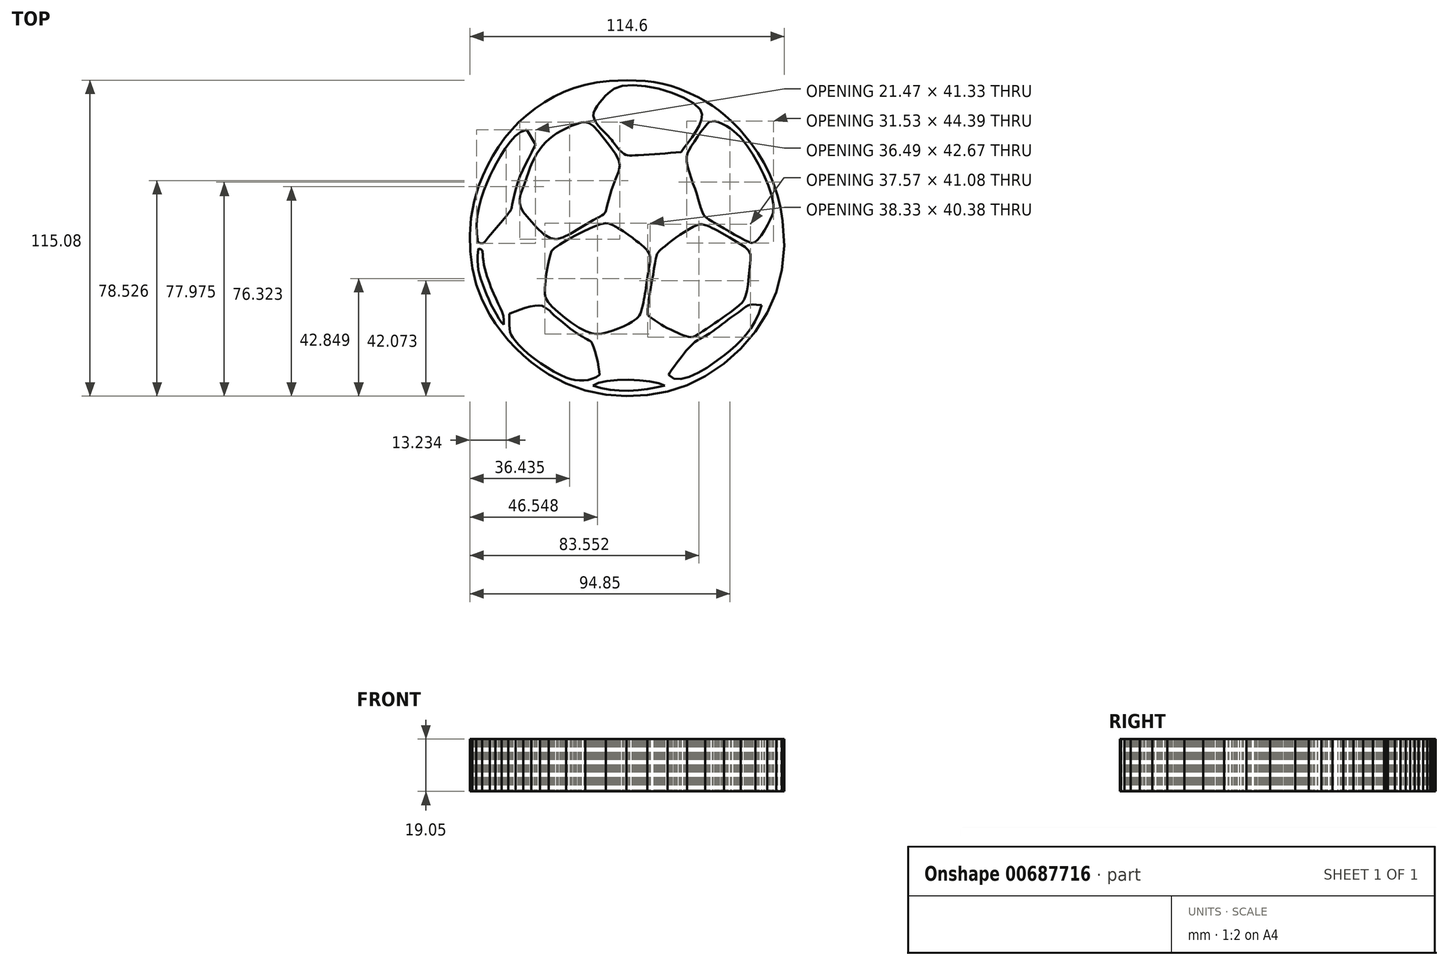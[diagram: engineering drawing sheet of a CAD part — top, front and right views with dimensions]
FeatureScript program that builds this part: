
annotation { "Feature Type Name" : "Feature", "Feature Type Description" : "" }
export const myFeature = defineFeature(function(context is Context, id is Id, definition is map)
    precondition{}
    {
        {
            var Q0;
            Q0=qCreatedBy(makeId("Top.planeOp"),FACE);
            var sketch = newSketch(context, id + "F0", { "sketchPlane" : qUnion([Q0])});
            skLineSegment(sketch, "E0", {"start": v(-6.43, 57.28) * mm, "end": v(-10.96, 56.75) * mm});
            skLineSegment(sketch, "E1", {"start": v(-10.96, 56.75) * mm, "end": v(-15.2, 55.9) * mm});
            skLineSegment(sketch, "E2", {"start": v(-15.2, 55.9) * mm, "end": v(-19.2, 54.74) * mm});
            skLineSegment(sketch, "E3", {"start": v(-19.2, 54.74) * mm, "end": v(-23, 53.29) * mm});
            skLineSegment(sketch, "E4", {"start": v(-23, 53.29) * mm, "end": v(-26.62, 51.54) * mm});
            skLineSegment(sketch, "E5", {"start": v(-26.62, 51.54) * mm, "end": v(-30.1, 49.5) * mm});
            skLineSegment(sketch, "E6", {"start": v(-30.1, 49.5) * mm, "end": v(-33.5, 47.2) * mm});
            skLineSegment(sketch, "E7", {"start": v(-33.5, 47.2) * mm, "end": v(-36.82, 44.64) * mm});
            skLineSegment(sketch, "E8", {"start": v(-36.82, 44.64) * mm, "end": v(-39.47, 42.27) * mm});
            skLineSegment(sketch, "E9", {"start": v(-39.47, 42.27) * mm, "end": v(-42.04, 39.56) * mm});
            skLineSegment(sketch, "E10", {"start": v(-42.04, 39.56) * mm, "end": v(-44.5, 36.54) * mm});
            skLineSegment(sketch, "E11", {"start": v(-44.5, 36.54) * mm, "end": v(-46.81, 33.3) * mm});
            skLineSegment(sketch, "E12", {"start": v(-46.81, 33.3) * mm, "end": v(-48.96, 29.86) * mm});
            skLineSegment(sketch, "E13", {"start": v(-48.96, 29.86) * mm, "end": v(-50.9, 26.3) * mm});
            skLineSegment(sketch, "E14", {"start": v(-50.9, 26.3) * mm, "end": v(-52.6, 22.69) * mm});
            skLineSegment(sketch, "E15", {"start": v(-52.6, 22.69) * mm, "end": v(-54.02, 19.06) * mm});
            skLineSegment(sketch, "E16", {"start": v(-54.02, 19.06) * mm, "end": v(-55.72, 13.29) * mm});
            skLineSegment(sketch, "E17", {"start": v(-55.72, 13.29) * mm, "end": v(-56.82, 7.32) * mm});
            skLineSegment(sketch, "E18", {"start": v(-56.82, 7.32) * mm, "end": v(-57.3, 1.24) * mm});
            skLineSegment(sketch, "E19", {"start": v(-57.3, 1.24) * mm, "end": v(-57.16, -4.87) * mm});
            skLineSegment(sketch, "E20", {"start": v(-57.16, -4.87) * mm, "end": v(-56.37, -10.92) * mm});
            skLineSegment(sketch, "E21", {"start": v(-56.37, -10.92) * mm, "end": v(-54.92, -16.83) * mm});
            skLineSegment(sketch, "E22", {"start": v(-54.92, -16.83) * mm, "end": v(-52.82, -22.52) * mm});
            skLineSegment(sketch, "E23", {"start": v(-52.82, -22.52) * mm, "end": v(-50.03, -27.9) * mm});
            skLineSegment(sketch, "E24", {"start": v(-50.03, -27.9) * mm, "end": v(-47.95, -31.1) * mm});
            skLineSegment(sketch, "E25", {"start": v(-47.95, -31.1) * mm, "end": v(-45.67, -34.2) * mm});
            skLineSegment(sketch, "E26", {"start": v(-45.67, -34.2) * mm, "end": v(-43.2, -37.17) * mm});
            skLineSegment(sketch, "E27", {"start": v(-43.2, -37.17) * mm, "end": v(-40.57, -40) * mm});
            skLineSegment(sketch, "E28", {"start": v(-40.57, -40) * mm, "end": v(-37.77, -42.66) * mm});
            skLineSegment(sketch, "E29", {"start": v(-37.77, -42.66) * mm, "end": v(-34.84, -45.16) * mm});
            skLineSegment(sketch, "E30", {"start": v(-34.84, -45.16) * mm, "end": v(-31.77, -47.49) * mm});
            skLineSegment(sketch, "E31", {"start": v(-31.77, -47.49) * mm, "end": v(-28.58, -49.63) * mm});
            skLineSegment(sketch, "E32", {"start": v(-28.58, -49.63) * mm, "end": v(-22.14, -53.01) * mm});
            skLineSegment(sketch, "E33", {"start": v(-22.14, -53.01) * mm, "end": v(-15.14, -55.46) * mm});
            skLineSegment(sketch, "E34", {"start": v(-15.14, -55.46) * mm, "end": v(-7.77, -56.97) * mm});
            skLineSegment(sketch, "E35", {"start": v(-7.77, -56.97) * mm, "end": v(-0.2, -57.54) * mm});
            skLineSegment(sketch, "E36", {"start": v(-0.2, -57.54) * mm, "end": v(7.4, -57.17) * mm});
            skLineSegment(sketch, "E37", {"start": v(7.4, -57.17) * mm, "end": v(14.82, -55.84) * mm});
            skLineSegment(sketch, "E38", {"start": v(14.82, -55.84) * mm, "end": v(21.9, -53.57) * mm});
            skLineSegment(sketch, "E39", {"start": v(21.9, -53.57) * mm, "end": v(28.46, -50.35) * mm});
            skLineSegment(sketch, "E40", {"start": v(28.46, -50.35) * mm, "end": v(35.3, -45.68) * mm});
            skLineSegment(sketch, "E41", {"start": v(35.3, -45.68) * mm, "end": v(41.42, -40.23) * mm});
            skLineSegment(sketch, "E42", {"start": v(41.42, -40.23) * mm, "end": v(46.71, -34.04) * mm});
            skLineSegment(sketch, "E43", {"start": v(46.71, -34.04) * mm, "end": v(51.06, -27.15) * mm});
            skLineSegment(sketch, "E44", {"start": v(51.06, -27.15) * mm, "end": v(54.35, -19.62) * mm});
            skLineSegment(sketch, "E45", {"start": v(54.35, -19.62) * mm, "end": v(56.47, -11.5) * mm});
            skLineSegment(sketch, "E46", {"start": v(56.47, -11.5) * mm, "end": v(57.3, -2.82) * mm});
            skLineSegment(sketch, "E47", {"start": v(57.3, -2.82) * mm, "end": v(56.73, 6.35) * mm});
            skLineSegment(sketch, "E48", {"start": v(56.73, 6.35) * mm, "end": v(55.88, 11.3) * mm});
            skLineSegment(sketch, "E49", {"start": v(55.88, 11.3) * mm, "end": v(54.78, 15.82) * mm});
            skLineSegment(sketch, "E50", {"start": v(54.78, 15.82) * mm, "end": v(53.41, 19.97) * mm});
            skLineSegment(sketch, "E51", {"start": v(53.41, 19.97) * mm, "end": v(51.77, 23.85) * mm});
            skLineSegment(sketch, "E52", {"start": v(51.77, 23.85) * mm, "end": v(49.84, 27.53) * mm});
            skLineSegment(sketch, "E53", {"start": v(49.84, 27.53) * mm, "end": v(47.6, 31.1) * mm});
            skLineSegment(sketch, "E54", {"start": v(47.6, 31.1) * mm, "end": v(45.06, 34.62) * mm});
            skLineSegment(sketch, "E55", {"start": v(45.06, 34.62) * mm, "end": v(42.2, 38.18) * mm});
            skLineSegment(sketch, "E56", {"start": v(42.2, 38.18) * mm, "end": v(41.76, 38.73) * mm});
            skLineSegment(sketch, "E57", {"start": v(41.76, 38.73) * mm, "end": v(41.43, 39.18) * mm});
            skLineSegment(sketch, "E58", {"start": v(41.43, 39.18) * mm, "end": v(41.26, 39.4) * mm});
            skLineSegment(sketch, "E59", {"start": v(41.26, 39.4) * mm, "end": v(41.07, 39.63) * mm});
            skLineSegment(sketch, "E60", {"start": v(41.07, 39.63) * mm, "end": v(40.85, 39.87) * mm});
            skLineSegment(sketch, "E61", {"start": v(40.85, 39.87) * mm, "end": v(40.58, 40.14) * mm});
            skLineSegment(sketch, "E62", {"start": v(40.58, 40.14) * mm, "end": v(37.99, 42.62) * mm});
            skLineSegment(sketch, "E63", {"start": v(37.99, 42.62) * mm, "end": v(35.66, 44.75) * mm});
            skLineSegment(sketch, "E64", {"start": v(35.66, 44.75) * mm, "end": v(33.45, 46.62) * mm});
            skLineSegment(sketch, "E65", {"start": v(33.45, 46.62) * mm, "end": v(31.21, 48.3) * mm});
            skLineSegment(sketch, "E66", {"start": v(31.21, 48.3) * mm, "end": v(28.79, 49.85) * mm});
            skLineSegment(sketch, "E67", {"start": v(28.79, 49.85) * mm, "end": v(26.03, 51.36) * mm});
            skLineSegment(sketch, "E68", {"start": v(26.03, 51.36) * mm, "end": v(22.78, 52.89) * mm});
            skLineSegment(sketch, "E69", {"start": v(22.78, 52.89) * mm, "end": v(18.9, 54.52) * mm});
            skLineSegment(sketch, "E70", {"start": v(18.9, 54.52) * mm, "end": v(16.04, 55.5) * mm});
            skLineSegment(sketch, "E71", {"start": v(16.04, 55.5) * mm, "end": v(13.02, 56.29) * mm});
            skLineSegment(sketch, "E72", {"start": v(13.02, 56.29) * mm, "end": v(9.86, 56.86) * mm});
            skLineSegment(sketch, "E73", {"start": v(9.86, 56.86) * mm, "end": v(6.63, 57.25) * mm});
            skLineSegment(sketch, "E74", {"start": v(6.63, 57.25) * mm, "end": v(3.34, 57.47) * mm});
            skLineSegment(sketch, "E75", {"start": v(3.34, 57.47) * mm, "end": v(0.04, 57.54) * mm});
            skLineSegment(sketch, "E76", {"start": v(0.04, 57.54) * mm, "end": v(-3.23, 57.47) * mm});
            skLineSegment(sketch, "E77", {"start": v(-3.23, 57.47) * mm, "end": v(-6.43, 57.28) * mm});
            skLineSegment(sketch, "E78", {"start": v(-7.9, 5.5) * mm, "end": v(-9.76, 5.04) * mm});
            skLineSegment(sketch, "E79", {"start": v(-9.76, 5.04) * mm, "end": v(-12.38, 4.05) * mm});
            skLineSegment(sketch, "E80", {"start": v(-12.38, 4.05) * mm, "end": v(-15.46, 2.67) * mm});
            skLineSegment(sketch, "E81", {"start": v(-15.46, 2.67) * mm, "end": v(-18.7, 1.06) * mm});
            skLineSegment(sketch, "E82", {"start": v(-18.7, 1.06) * mm, "end": v(-21.82, -0.64) * mm});
            skLineSegment(sketch, "E83", {"start": v(-21.82, -0.64) * mm, "end": v(-24.53, -2.26) * mm});
            skLineSegment(sketch, "E84", {"start": v(-24.53, -2.26) * mm, "end": v(-26.52, -3.67) * mm});
            skLineSegment(sketch, "E85", {"start": v(-26.52, -3.67) * mm, "end": v(-27.5, -4.7) * mm});
            skLineSegment(sketch, "E86", {"start": v(-27.5, -4.7) * mm, "end": v(-27.94, -5.93) * mm});
            skLineSegment(sketch, "E87", {"start": v(-27.94, -5.93) * mm, "end": v(-28.43, -7.85) * mm});
            skLineSegment(sketch, "E88", {"start": v(-28.43, -7.85) * mm, "end": v(-28.93, -10.24) * mm});
            skLineSegment(sketch, "E89", {"start": v(-28.93, -10.24) * mm, "end": v(-29.37, -12.9) * mm});
            skLineSegment(sketch, "E90", {"start": v(-29.37, -12.9) * mm, "end": v(-29.72, -15.6) * mm});
            skLineSegment(sketch, "E91", {"start": v(-29.72, -15.6) * mm, "end": v(-29.92, -18.13) * mm});
            skLineSegment(sketch, "E92", {"start": v(-29.92, -18.13) * mm, "end": v(-29.9, -20.26) * mm});
            skLineSegment(sketch, "E93", {"start": v(-29.9, -20.26) * mm, "end": v(-29.64, -21.77) * mm});
            skLineSegment(sketch, "E94", {"start": v(-29.64, -21.77) * mm, "end": v(-28.79, -23.23) * mm});
            skLineSegment(sketch, "E95", {"start": v(-28.79, -23.23) * mm, "end": v(-27.24, -25.01) * mm});
            skLineSegment(sketch, "E96", {"start": v(-27.24, -25.01) * mm, "end": v(-25.16, -26.98) * mm});
            skLineSegment(sketch, "E97", {"start": v(-25.16, -26.98) * mm, "end": v(-22.73, -28.98) * mm});
            skLineSegment(sketch, "E98", {"start": v(-22.73, -28.98) * mm, "end": v(-20.12, -30.9) * mm});
            skLineSegment(sketch, "E99", {"start": v(-20.12, -30.9) * mm, "end": v(-17.48, -32.57) * mm});
            skLineSegment(sketch, "E100", {"start": v(-17.48, -32.57) * mm, "end": v(-15, -33.88) * mm});
            skLineSegment(sketch, "E101", {"start": v(-15, -33.88) * mm, "end": v(-12.84, -34.68) * mm});
            skLineSegment(sketch, "E102", {"start": v(-12.84, -34.68) * mm, "end": v(-11.16, -34.88) * mm});
            skLineSegment(sketch, "E103", {"start": v(-11.16, -34.88) * mm, "end": v(-9.25, -34.74) * mm});
            skLineSegment(sketch, "E104", {"start": v(-9.25, -34.74) * mm, "end": v(-7.2, -34.32) * mm});
            skLineSegment(sketch, "E105", {"start": v(-7.2, -34.32) * mm, "end": v(-5.11, -33.7) * mm});
            skLineSegment(sketch, "E106", {"start": v(-5.11, -33.7) * mm, "end": v(-3.08, -32.92) * mm});
            skLineSegment(sketch, "E107", {"start": v(-3.08, -32.92) * mm, "end": v(-1.18, -32.08) * mm});
            skLineSegment(sketch, "E108", {"start": v(-1.18, -32.08) * mm, "end": v(0.48, -31.23) * mm});
            skLineSegment(sketch, "E109", {"start": v(0.48, -31.23) * mm, "end": v(1.82, -30.44) * mm});
            skLineSegment(sketch, "E110", {"start": v(1.82, -30.44) * mm, "end": v(2.73, -29.84) * mm});
            skLineSegment(sketch, "E111", {"start": v(2.73, -29.84) * mm, "end": v(3.45, -29.3) * mm});
            skLineSegment(sketch, "E112", {"start": v(3.45, -29.3) * mm, "end": v(4.02, -28.78) * mm});
            skLineSegment(sketch, "E113", {"start": v(4.02, -28.78) * mm, "end": v(4.46, -28.22) * mm});
            skLineSegment(sketch, "E114", {"start": v(4.46, -28.22) * mm, "end": v(4.82, -27.56) * mm});
            skLineSegment(sketch, "E115", {"start": v(4.82, -27.56) * mm, "end": v(5.13, -26.74) * mm});
            skLineSegment(sketch, "E116", {"start": v(5.13, -26.74) * mm, "end": v(5.42, -25.73) * mm});
            skLineSegment(sketch, "E117", {"start": v(5.42, -25.73) * mm, "end": v(5.73, -24.45) * mm});
            skLineSegment(sketch, "E118", {"start": v(5.73, -24.45) * mm, "end": v(5.96, -23.4) * mm});
            skLineSegment(sketch, "E119", {"start": v(5.96, -23.4) * mm, "end": v(6.17, -22.34) * mm});
            skLineSegment(sketch, "E120", {"start": v(6.17, -22.34) * mm, "end": v(6.36, -21.29) * mm});
            skLineSegment(sketch, "E121", {"start": v(6.36, -21.29) * mm, "end": v(6.54, -20.23) * mm});
            skLineSegment(sketch, "E122", {"start": v(6.54, -20.23) * mm, "end": v(6.7, -19.17) * mm});
            skLineSegment(sketch, "E123", {"start": v(6.7, -19.17) * mm, "end": v(6.87, -18.11) * mm});
            skLineSegment(sketch, "E124", {"start": v(6.87, -18.11) * mm, "end": v(7.02, -17.05) * mm});
            skLineSegment(sketch, "E125", {"start": v(7.02, -17.05) * mm, "end": v(7.16, -16) * mm});
            skLineSegment(sketch, "E126", {"start": v(7.16, -16) * mm, "end": v(7.65, -12.86) * mm});
            skLineSegment(sketch, "E127", {"start": v(7.65, -12.86) * mm, "end": v(8.09, -10.41) * mm});
            skLineSegment(sketch, "E128", {"start": v(8.09, -10.41) * mm, "end": v(8.37, -8.5) * mm});
            skLineSegment(sketch, "E129", {"start": v(8.37, -8.5) * mm, "end": v(8.41, -6.98) * mm});
            skLineSegment(sketch, "E130", {"start": v(8.41, -6.98) * mm, "end": v(8.12, -5.7) * mm});
            skLineSegment(sketch, "E131", {"start": v(8.12, -5.7) * mm, "end": v(7.4, -4.48) * mm});
            skLineSegment(sketch, "E132", {"start": v(7.4, -4.48) * mm, "end": v(6.16, -3.2) * mm});
            skLineSegment(sketch, "E133", {"start": v(6.16, -3.2) * mm, "end": v(4.31, -1.68) * mm});
            skLineSegment(sketch, "E134", {"start": v(4.31, -1.68) * mm, "end": v(3.38, -0.95) * mm});
            skLineSegment(sketch, "E135", {"start": v(3.38, -0.95) * mm, "end": v(2.04, 0.08) * mm});
            skLineSegment(sketch, "E136", {"start": v(2.04, 0.08) * mm, "end": v(0.42, 1.3) * mm});
            skLineSegment(sketch, "E137", {"start": v(0.42, 1.3) * mm, "end": v(-1.38, 2.56) * mm});
            skLineSegment(sketch, "E138", {"start": v(-1.38, 2.56) * mm, "end": v(-3.23, 3.74) * mm});
            skLineSegment(sketch, "E139", {"start": v(-3.23, 3.74) * mm, "end": v(-5, 4.7) * mm});
            skLineSegment(sketch, "E140", {"start": v(-5, 4.7) * mm, "end": v(-6.6, 5.34) * mm});
            skLineSegment(sketch, "E141", {"start": v(-6.6, 5.34) * mm, "end": v(-7.9, 5.5) * mm});
            skLineSegment(sketch, "E142", {"start": v(25.64, 4.87) * mm, "end": v(24.21, 4.2) * mm});
            skLineSegment(sketch, "E143", {"start": v(24.21, 4.2) * mm, "end": v(22.63, 3.34) * mm});
            skLineSegment(sketch, "E144", {"start": v(22.63, 3.34) * mm, "end": v(20.97, 2.33) * mm});
            skLineSegment(sketch, "E145", {"start": v(20.97, 2.33) * mm, "end": v(19.3, 1.24) * mm});
            skLineSegment(sketch, "E146", {"start": v(19.3, 1.24) * mm, "end": v(17.67, 0.13) * mm});
            skLineSegment(sketch, "E147", {"start": v(17.67, 0.13) * mm, "end": v(16.18, -0.96) * mm});
            skLineSegment(sketch, "E148", {"start": v(16.18, -0.96) * mm, "end": v(14.88, -1.98) * mm});
            skLineSegment(sketch, "E149", {"start": v(14.88, -1.98) * mm, "end": v(13.84, -2.85) * mm});
            skLineSegment(sketch, "E150", {"start": v(13.84, -2.85) * mm, "end": v(12.97, -3.6) * mm});
            skLineSegment(sketch, "E151", {"start": v(12.97, -3.6) * mm, "end": v(12.28, -4.17) * mm});
            skLineSegment(sketch, "E152", {"start": v(12.28, -4.17) * mm, "end": v(11.74, -4.65) * mm});
            skLineSegment(sketch, "E153", {"start": v(11.74, -4.65) * mm, "end": v(11.32, -5.15) * mm});
            skLineSegment(sketch, "E154", {"start": v(11.32, -5.15) * mm, "end": v(10.98, -5.75) * mm});
            skLineSegment(sketch, "E155", {"start": v(10.98, -5.75) * mm, "end": v(10.7, -6.55) * mm});
            skLineSegment(sketch, "E156", {"start": v(10.7, -6.55) * mm, "end": v(10.45, -7.64) * mm});
            skLineSegment(sketch, "E157", {"start": v(10.45, -7.64) * mm, "end": v(10.19, -9.12) * mm});
            skLineSegment(sketch, "E158", {"start": v(10.19, -9.12) * mm, "end": v(9.87, -11) * mm});
            skLineSegment(sketch, "E159", {"start": v(9.87, -11) * mm, "end": v(9.5, -13.15) * mm});
            skLineSegment(sketch, "E160", {"start": v(9.5, -13.15) * mm, "end": v(9.1, -15.47) * mm});
            skLineSegment(sketch, "E161", {"start": v(9.1, -15.47) * mm, "end": v(8.69, -17.88) * mm});
            skLineSegment(sketch, "E162", {"start": v(8.69, -17.88) * mm, "end": v(8.3, -20.26) * mm});
            skLineSegment(sketch, "E163", {"start": v(8.3, -20.26) * mm, "end": v(7.95, -22.52) * mm});
            skLineSegment(sketch, "E164", {"start": v(7.95, -22.52) * mm, "end": v(7.67, -24.56) * mm});
            skLineSegment(sketch, "E165", {"start": v(7.67, -24.56) * mm, "end": v(7.5, -26.3) * mm});
            skLineSegment(sketch, "E166", {"start": v(7.5, -26.3) * mm, "end": v(7.47, -26.91) * mm});
            skLineSegment(sketch, "E167", {"start": v(7.47, -26.91) * mm, "end": v(7.48, -27.38) * mm});
            skLineSegment(sketch, "E168", {"start": v(7.48, -27.38) * mm, "end": v(7.55, -27.74) * mm});
            skLineSegment(sketch, "E169", {"start": v(7.55, -27.74) * mm, "end": v(7.69, -28.03) * mm});
            skLineSegment(sketch, "E170", {"start": v(7.69, -28.03) * mm, "end": v(7.89, -28.27) * mm});
            skLineSegment(sketch, "E171", {"start": v(7.89, -28.27) * mm, "end": v(8.16, -28.51) * mm});
            skLineSegment(sketch, "E172", {"start": v(8.16, -28.51) * mm, "end": v(8.52, -28.78) * mm});
            skLineSegment(sketch, "E173", {"start": v(8.52, -28.78) * mm, "end": v(8.97, -29.1) * mm});
            skLineSegment(sketch, "E174", {"start": v(8.97, -29.1) * mm, "end": v(10.18, -30) * mm});
            skLineSegment(sketch, "E175", {"start": v(10.18, -30) * mm, "end": v(11.33, -30.78) * mm});
            skLineSegment(sketch, "E176", {"start": v(11.33, -30.78) * mm, "end": v(12.44, -31.47) * mm});
            skLineSegment(sketch, "E177", {"start": v(12.44, -31.47) * mm, "end": v(13.54, -32.1) * mm});
            skLineSegment(sketch, "E178", {"start": v(13.54, -32.1) * mm, "end": v(14.67, -32.7) * mm});
            skLineSegment(sketch, "E179", {"start": v(14.67, -32.7) * mm, "end": v(15.87, -33.29) * mm});
            skLineSegment(sketch, "E180", {"start": v(15.87, -33.29) * mm, "end": v(17.16, -33.89) * mm});
            skLineSegment(sketch, "E181", {"start": v(17.16, -33.89) * mm, "end": v(18.59, -34.53) * mm});
            skLineSegment(sketch, "E182", {"start": v(18.59, -34.53) * mm, "end": v(19.6, -34.98) * mm});
            skLineSegment(sketch, "E183", {"start": v(19.6, -34.98) * mm, "end": v(20.55, -35.4) * mm});
            skLineSegment(sketch, "E184", {"start": v(20.55, -35.4) * mm, "end": v(21.46, -35.73) * mm});
            skLineSegment(sketch, "E185", {"start": v(21.46, -35.73) * mm, "end": v(22.35, -35.94) * mm});
            skLineSegment(sketch, "E186", {"start": v(22.35, -35.94) * mm, "end": v(23.24, -36) * mm});
            skLineSegment(sketch, "E187", {"start": v(23.24, -36) * mm, "end": v(24.15, -35.89) * mm});
            skLineSegment(sketch, "E188", {"start": v(24.15, -35.89) * mm, "end": v(25.1, -35.55) * mm});
            skLineSegment(sketch, "E189", {"start": v(25.1, -35.55) * mm, "end": v(26.13, -34.95) * mm});
            skLineSegment(sketch, "E190", {"start": v(26.13, -34.95) * mm, "end": v(27.59, -33.95) * mm});
            skLineSegment(sketch, "E191", {"start": v(27.59, -33.95) * mm, "end": v(29.03, -32.96) * mm});
            skLineSegment(sketch, "E192", {"start": v(29.03, -32.96) * mm, "end": v(30.46, -32) * mm});
            skLineSegment(sketch, "E193", {"start": v(30.46, -32) * mm, "end": v(31.88, -31.02) * mm});
            skLineSegment(sketch, "E194", {"start": v(31.88, -31.02) * mm, "end": v(33.3, -30.05) * mm});
            skLineSegment(sketch, "E195", {"start": v(33.3, -30.05) * mm, "end": v(34.72, -29.06) * mm});
            skLineSegment(sketch, "E196", {"start": v(34.72, -29.06) * mm, "end": v(36.14, -28.04) * mm});
            skLineSegment(sketch, "E197", {"start": v(36.14, -28.04) * mm, "end": v(37.57, -26.99) * mm});
            skLineSegment(sketch, "E198", {"start": v(37.57, -26.99) * mm, "end": v(39.4, -25.62) * mm});
            skLineSegment(sketch, "E199", {"start": v(39.4, -25.62) * mm, "end": v(40.82, -24.5) * mm});
            skLineSegment(sketch, "E200", {"start": v(40.82, -24.5) * mm, "end": v(41.9, -23.45) * mm});
            skLineSegment(sketch, "E201", {"start": v(41.9, -23.45) * mm, "end": v(42.69, -22.33) * mm});
            skLineSegment(sketch, "E202", {"start": v(42.69, -22.33) * mm, "end": v(43.27, -20.97) * mm});
            skLineSegment(sketch, "E203", {"start": v(43.27, -20.97) * mm, "end": v(43.7, -19.22) * mm});
            skLineSegment(sketch, "E204", {"start": v(43.7, -19.22) * mm, "end": v(44.05, -16.92) * mm});
            skLineSegment(sketch, "E205", {"start": v(44.05, -16.92) * mm, "end": v(44.38, -13.9) * mm});
            skLineSegment(sketch, "E206", {"start": v(44.38, -13.9) * mm, "end": v(44.78, -10.4) * mm});
            skLineSegment(sketch, "E207", {"start": v(44.78, -10.4) * mm, "end": v(45.04, -7.86) * mm});
            skLineSegment(sketch, "E208", {"start": v(45.04, -7.86) * mm, "end": v(44.95, -6) * mm});
            skLineSegment(sketch, "E209", {"start": v(44.95, -6) * mm, "end": v(44.34, -4.56) * mm});
            skLineSegment(sketch, "E210", {"start": v(44.34, -4.56) * mm, "end": v(43, -3.23) * mm});
            skLineSegment(sketch, "E211", {"start": v(43, -3.23) * mm, "end": v(40.72, -1.73) * mm});
            skLineSegment(sketch, "E212", {"start": v(40.72, -1.73) * mm, "end": v(37.33, 0.2) * mm});
            skLineSegment(sketch, "E213", {"start": v(37.33, 0.2) * mm, "end": v(32.63, 2.87) * mm});
            skLineSegment(sketch, "E214", {"start": v(32.63, 2.87) * mm, "end": v(31.88, 3.3) * mm});
            skLineSegment(sketch, "E215", {"start": v(31.88, 3.3) * mm, "end": v(31.05, 3.75) * mm});
            skLineSegment(sketch, "E216", {"start": v(31.05, 3.75) * mm, "end": v(30.15, 4.2) * mm});
            skLineSegment(sketch, "E217", {"start": v(30.15, 4.2) * mm, "end": v(29.22, 4.59) * mm});
            skLineSegment(sketch, "E218", {"start": v(29.22, 4.59) * mm, "end": v(28.28, 4.9) * mm});
            skLineSegment(sketch, "E219", {"start": v(28.28, 4.9) * mm, "end": v(27.35, 5.07) * mm});
            skLineSegment(sketch, "E220", {"start": v(27.35, 5.07) * mm, "end": v(26.47, 5.07) * mm});
            skLineSegment(sketch, "E221", {"start": v(26.47, 5.07) * mm, "end": v(25.64, 4.87) * mm});
            skLineSegment(sketch, "E222", {"start": v(-16.67, 42.17) * mm, "end": v(-18.57, 41.59) * mm});
            skLineSegment(sketch, "E223", {"start": v(-18.57, 41.59) * mm, "end": v(-20.43, 40.88) * mm});
            skLineSegment(sketch, "E224", {"start": v(-20.43, 40.88) * mm, "end": v(-22.22, 40.07) * mm});
            skLineSegment(sketch, "E225", {"start": v(-22.22, 40.07) * mm, "end": v(-23.94, 39.18) * mm});
            skLineSegment(sketch, "E226", {"start": v(-23.94, 39.18) * mm, "end": v(-25.56, 38.2) * mm});
            skLineSegment(sketch, "E227", {"start": v(-25.56, 38.2) * mm, "end": v(-27.05, 37.18) * mm});
            skLineSegment(sketch, "E228", {"start": v(-27.05, 37.18) * mm, "end": v(-28.4, 36.1) * mm});
            skLineSegment(sketch, "E229", {"start": v(-28.4, 36.1) * mm, "end": v(-29.56, 35.01) * mm});
            skLineSegment(sketch, "E230", {"start": v(-29.56, 35.01) * mm, "end": v(-30.77, 33.68) * mm});
            skLineSegment(sketch, "E231", {"start": v(-30.77, 33.68) * mm, "end": v(-31.84, 32.3) * mm});
            skLineSegment(sketch, "E232", {"start": v(-31.84, 32.3) * mm, "end": v(-32.8, 30.84) * mm});
            skLineSegment(sketch, "E233", {"start": v(-32.8, 30.84) * mm, "end": v(-33.66, 29.3) * mm});
            skLineSegment(sketch, "E234", {"start": v(-33.66, 29.3) * mm, "end": v(-34.46, 27.66) * mm});
            skLineSegment(sketch, "E235", {"start": v(-34.46, 27.66) * mm, "end": v(-35.2, 25.9) * mm});
            skLineSegment(sketch, "E236", {"start": v(-35.2, 25.9) * mm, "end": v(-35.94, 23.98) * mm});
            skLineSegment(sketch, "E237", {"start": v(-35.94, 23.98) * mm, "end": v(-36.66, 21.91) * mm});
            skLineSegment(sketch, "E238", {"start": v(-36.66, 21.91) * mm, "end": v(-37.48, 19.62) * mm});
            skLineSegment(sketch, "E239", {"start": v(-37.48, 19.62) * mm, "end": v(-38.22, 17.66) * mm});
            skLineSegment(sketch, "E240", {"start": v(-38.22, 17.66) * mm, "end": v(-38.78, 15.93) * mm});
            skLineSegment(sketch, "E241", {"start": v(-38.78, 15.93) * mm, "end": v(-39.1, 14.36) * mm});
            skLineSegment(sketch, "E242", {"start": v(-39.1, 14.36) * mm, "end": v(-39.11, 12.86) * mm});
            skLineSegment(sketch, "E243", {"start": v(-39.11, 12.86) * mm, "end": v(-38.72, 11.33) * mm});
            skLineSegment(sketch, "E244", {"start": v(-38.72, 11.33) * mm, "end": v(-37.87, 9.69) * mm});
            skLineSegment(sketch, "E245", {"start": v(-37.87, 9.69) * mm, "end": v(-36.47, 7.86) * mm});
            skLineSegment(sketch, "E246", {"start": v(-36.47, 7.86) * mm, "end": v(-33.01, 4) * mm});
            skLineSegment(sketch, "E247", {"start": v(-33.01, 4) * mm, "end": v(-30.28, 1.42) * mm});
            skLineSegment(sketch, "E248", {"start": v(-30.28, 1.42) * mm, "end": v(-27.96, 0) * mm});
            skLineSegment(sketch, "E249", {"start": v(-27.96, 0) * mm, "end": v(-25.77, -0.35) * mm});
            skLineSegment(sketch, "E250", {"start": v(-25.77, -0.35) * mm, "end": v(-23.4, 0.25) * mm});
            skLineSegment(sketch, "E251", {"start": v(-23.4, 0.25) * mm, "end": v(-20.56, 1.68) * mm});
            skLineSegment(sketch, "E252", {"start": v(-20.56, 1.68) * mm, "end": v(-16.95, 3.84) * mm});
            skLineSegment(sketch, "E253", {"start": v(-16.95, 3.84) * mm, "end": v(-12.26, 6.61) * mm});
            skLineSegment(sketch, "E254", {"start": v(-12.26, 6.61) * mm, "end": v(-11.83, 6.85) * mm});
            skLineSegment(sketch, "E255", {"start": v(-11.83, 6.85) * mm, "end": v(-11.42, 7.07) * mm});
            skLineSegment(sketch, "E256", {"start": v(-11.42, 7.07) * mm, "end": v(-11.04, 7.27) * mm});
            skLineSegment(sketch, "E257", {"start": v(-11.04, 7.27) * mm, "end": v(-10.67, 7.46) * mm});
            skLineSegment(sketch, "E258", {"start": v(-10.67, 7.46) * mm, "end": v(-10.3, 7.65) * mm});
            skLineSegment(sketch, "E259", {"start": v(-10.3, 7.65) * mm, "end": v(-9.93, 7.84) * mm});
            skLineSegment(sketch, "E260", {"start": v(-9.93, 7.84) * mm, "end": v(-9.56, 8.05) * mm});
            skLineSegment(sketch, "E261", {"start": v(-9.56, 8.05) * mm, "end": v(-9.17, 8.28) * mm});
            skLineSegment(sketch, "E262", {"start": v(-9.17, 8.28) * mm, "end": v(-8.66, 8.61) * mm});
            skLineSegment(sketch, "E263", {"start": v(-8.66, 8.61) * mm, "end": v(-8.3, 8.92) * mm});
            skLineSegment(sketch, "E264", {"start": v(-8.3, 8.92) * mm, "end": v(-8.05, 9.22) * mm});
            skLineSegment(sketch, "E265", {"start": v(-8.05, 9.22) * mm, "end": v(-7.87, 9.54) * mm});
            skLineSegment(sketch, "E266", {"start": v(-7.87, 9.54) * mm, "end": v(-7.75, 9.92) * mm});
            skLineSegment(sketch, "E267", {"start": v(-7.75, 9.92) * mm, "end": v(-7.64, 10.37) * mm});
            skLineSegment(sketch, "E268", {"start": v(-7.64, 10.37) * mm, "end": v(-7.52, 10.93) * mm});
            skLineSegment(sketch, "E269", {"start": v(-7.52, 10.93) * mm, "end": v(-7.36, 11.61) * mm});
            skLineSegment(sketch, "E270", {"start": v(-7.36, 11.61) * mm, "end": v(-5.62, 17.5) * mm});
            skLineSegment(sketch, "E271", {"start": v(-5.62, 17.5) * mm, "end": v(-4.13, 21.6) * mm});
            skLineSegment(sketch, "E272", {"start": v(-4.13, 21.6) * mm, "end": v(-3.07, 24.42) * mm});
            skLineSegment(sketch, "E273", {"start": v(-3.07, 24.42) * mm, "end": v(-2.62, 26.55) * mm});
            skLineSegment(sketch, "E274", {"start": v(-2.62, 26.55) * mm, "end": v(-2.96, 28.5) * mm});
            skLineSegment(sketch, "E275", {"start": v(-2.96, 28.5) * mm, "end": v(-4.28, 30.86) * mm});
            skLineSegment(sketch, "E276", {"start": v(-4.28, 30.86) * mm, "end": v(-6.75, 34.16) * mm});
            skLineSegment(sketch, "E277", {"start": v(-6.75, 34.16) * mm, "end": v(-10.55, 38.94) * mm});
            skLineSegment(sketch, "E278", {"start": v(-10.55, 38.94) * mm, "end": v(-11.05, 39.56) * mm});
            skLineSegment(sketch, "E279", {"start": v(-11.05, 39.56) * mm, "end": v(-11.63, 40.21) * mm});
            skLineSegment(sketch, "E280", {"start": v(-11.63, 40.21) * mm, "end": v(-12.29, 40.85) * mm});
            skLineSegment(sketch, "E281", {"start": v(-12.29, 40.85) * mm, "end": v(-13.02, 41.43) * mm});
            skLineSegment(sketch, "E282", {"start": v(-13.02, 41.43) * mm, "end": v(-13.82, 41.9) * mm});
            skLineSegment(sketch, "E283", {"start": v(-13.82, 41.9) * mm, "end": v(-14.7, 42.21) * mm});
            skLineSegment(sketch, "E284", {"start": v(-14.7, 42.21) * mm, "end": v(-15.65, 42.32) * mm});
            skLineSegment(sketch, "E285", {"start": v(-15.65, 42.32) * mm, "end": v(-16.67, 42.17) * mm});
            skLineSegment(sketch, "E286", {"start": v(30.04, 42.4) * mm, "end": v(29.26, 41.68) * mm});
            skLineSegment(sketch, "E287", {"start": v(29.26, 41.68) * mm, "end": v(28.21, 40.43) * mm});
            skLineSegment(sketch, "E288", {"start": v(28.21, 40.43) * mm, "end": v(27, 38.83) * mm});
            skLineSegment(sketch, "E289", {"start": v(27, 38.83) * mm, "end": v(25.74, 37.02) * mm});
            skLineSegment(sketch, "E290", {"start": v(25.74, 37.02) * mm, "end": v(24.53, 35.2) * mm});
            skLineSegment(sketch, "E291", {"start": v(24.53, 35.2) * mm, "end": v(23.45, 33.51) * mm});
            skLineSegment(sketch, "E292", {"start": v(23.45, 33.51) * mm, "end": v(22.63, 32.14) * mm});
            skLineSegment(sketch, "E293", {"start": v(22.63, 32.14) * mm, "end": v(22.15, 31.24) * mm});
            skLineSegment(sketch, "E294", {"start": v(22.15, 31.24) * mm, "end": v(21.78, 29.75) * mm});
            skLineSegment(sketch, "E295", {"start": v(21.78, 29.75) * mm, "end": v(21.81, 27.96) * mm});
            skLineSegment(sketch, "E296", {"start": v(21.81, 27.96) * mm, "end": v(22.15, 25.97) * mm});
            skLineSegment(sketch, "E297", {"start": v(22.15, 25.97) * mm, "end": v(22.7, 23.88) * mm});
            skLineSegment(sketch, "E298", {"start": v(22.7, 23.88) * mm, "end": v(23.38, 21.8) * mm});
            skLineSegment(sketch, "E299", {"start": v(23.38, 21.8) * mm, "end": v(24.1, 19.8) * mm});
            skLineSegment(sketch, "E300", {"start": v(24.1, 19.8) * mm, "end": v(24.75, 18) * mm});
            skLineSegment(sketch, "E301", {"start": v(24.75, 18) * mm, "end": v(25.25, 16.5) * mm});
            skLineSegment(sketch, "E302", {"start": v(25.25, 16.5) * mm, "end": v(26.18, 13.39) * mm});
            skLineSegment(sketch, "E303", {"start": v(26.18, 13.39) * mm, "end": v(26.88, 11.13) * mm});
            skLineSegment(sketch, "E304", {"start": v(26.88, 11.13) * mm, "end": v(27.45, 9.54) * mm});
            skLineSegment(sketch, "E305", {"start": v(27.45, 9.54) * mm, "end": v(28.03, 8.43) * mm});
            skLineSegment(sketch, "E306", {"start": v(28.03, 8.43) * mm, "end": v(28.74, 7.62) * mm});
            skLineSegment(sketch, "E307", {"start": v(28.74, 7.62) * mm, "end": v(29.7, 6.9) * mm});
            skLineSegment(sketch, "E308", {"start": v(29.7, 6.9) * mm, "end": v(31.02, 6.11) * mm});
            skLineSegment(sketch, "E309", {"start": v(31.02, 6.11) * mm, "end": v(32.83, 5.05) * mm});
            skLineSegment(sketch, "E310", {"start": v(32.83, 5.05) * mm, "end": v(33.8, 4.47) * mm});
            skLineSegment(sketch, "E311", {"start": v(33.8, 4.47) * mm, "end": v(35.29, 3.58) * mm});
            skLineSegment(sketch, "E312", {"start": v(35.29, 3.58) * mm, "end": v(37.14, 2.5) * mm});
            skLineSegment(sketch, "E313", {"start": v(37.14, 2.5) * mm, "end": v(39.16, 1.33) * mm});
            skLineSegment(sketch, "E314", {"start": v(39.16, 1.33) * mm, "end": v(41.18, 0.21) * mm});
            skLineSegment(sketch, "E315", {"start": v(41.18, 0.21) * mm, "end": v(43.02, -0.76) * mm});
            skLineSegment(sketch, "E316", {"start": v(43.02, -0.76) * mm, "end": v(44.5, -1.45) * mm});
            skLineSegment(sketch, "E317", {"start": v(44.5, -1.45) * mm, "end": v(45.44, -1.76) * mm});
            skLineSegment(sketch, "E318", {"start": v(45.44, -1.76) * mm, "end": v(46.5, -1.47) * mm});
            skLineSegment(sketch, "E319", {"start": v(46.5, -1.47) * mm, "end": v(47.7, -0.47) * mm});
            skLineSegment(sketch, "E320", {"start": v(47.7, -0.47) * mm, "end": v(48.93, 1.03) * mm});
            skLineSegment(sketch, "E321", {"start": v(48.93, 1.03) * mm, "end": v(50.13, 2.84) * mm});
            skLineSegment(sketch, "E322", {"start": v(50.13, 2.84) * mm, "end": v(51.23, 4.77) * mm});
            skLineSegment(sketch, "E323", {"start": v(51.23, 4.77) * mm, "end": v(52.16, 6.62) * mm});
            skLineSegment(sketch, "E324", {"start": v(52.16, 6.62) * mm, "end": v(52.84, 8.2) * mm});
            skLineSegment(sketch, "E325", {"start": v(52.84, 8.2) * mm, "end": v(53.2, 9.33) * mm});
            skLineSegment(sketch, "E326", {"start": v(53.2, 9.33) * mm, "end": v(53.32, 12.18) * mm});
            skLineSegment(sketch, "E327", {"start": v(53.32, 12.18) * mm, "end": v(52.7, 15.55) * mm});
            skLineSegment(sketch, "E328", {"start": v(52.7, 15.55) * mm, "end": v(51.48, 19.27) * mm});
            skLineSegment(sketch, "E329", {"start": v(51.48, 19.27) * mm, "end": v(49.83, 23.11) * mm});
            skLineSegment(sketch, "E330", {"start": v(49.83, 23.11) * mm, "end": v(47.9, 26.9) * mm});
            skLineSegment(sketch, "E331", {"start": v(47.9, 26.9) * mm, "end": v(45.85, 30.45) * mm});
            skLineSegment(sketch, "E332", {"start": v(45.85, 30.45) * mm, "end": v(43.83, 33.55) * mm});
            skLineSegment(sketch, "E333", {"start": v(43.83, 33.55) * mm, "end": v(42, 36.01) * mm});
            skLineSegment(sketch, "E334", {"start": v(42, 36.01) * mm, "end": v(41.14, 36.98) * mm});
            skLineSegment(sketch, "E335", {"start": v(41.14, 36.98) * mm, "end": v(40.1, 38) * mm});
            skLineSegment(sketch, "E336", {"start": v(40.1, 38) * mm, "end": v(38.9, 39.03) * mm});
            skLineSegment(sketch, "E337", {"start": v(38.9, 39.03) * mm, "end": v(37.59, 40.03) * mm});
            skLineSegment(sketch, "E338", {"start": v(37.59, 40.03) * mm, "end": v(36.2, 40.93) * mm});
            skLineSegment(sketch, "E339", {"start": v(36.2, 40.93) * mm, "end": v(34.77, 41.7) * mm});
            skLineSegment(sketch, "E340", {"start": v(34.77, 41.7) * mm, "end": v(33.34, 42.29) * mm});
            skLineSegment(sketch, "E341", {"start": v(33.34, 42.29) * mm, "end": v(31.94, 42.63) * mm});
            skLineSegment(sketch, "E342", {"start": v(31.94, 42.63) * mm, "end": v(30.04, 42.4) * mm});
            skLineSegment(sketch, "E343", {"start": v(19.77, 31.43) * mm, "end": v(20.77, 32.88) * mm});
            skLineSegment(sketch, "E344", {"start": v(20.77, 32.88) * mm, "end": v(22.12, 34.66) * mm});
            skLineSegment(sketch, "E345", {"start": v(22.12, 34.66) * mm, "end": v(23.63, 36.67) * mm});
            skLineSegment(sketch, "E346", {"start": v(23.63, 36.67) * mm, "end": v(25.1, 38.82) * mm});
            skLineSegment(sketch, "E347", {"start": v(25.1, 38.82) * mm, "end": v(26.32, 41) * mm});
            skLineSegment(sketch, "E348", {"start": v(26.32, 41) * mm, "end": v(27.12, 43.13) * mm});
            skLineSegment(sketch, "E349", {"start": v(27.12, 43.13) * mm, "end": v(27.3, 45.1) * mm});
            skLineSegment(sketch, "E350", {"start": v(27.3, 45.1) * mm, "end": v(26.65, 46.8) * mm});
            skLineSegment(sketch, "E351", {"start": v(26.65, 46.8) * mm, "end": v(24.26, 49.11) * mm});
            skLineSegment(sketch, "E352", {"start": v(24.26, 49.11) * mm, "end": v(20.7, 51.21) * mm});
            skLineSegment(sketch, "E353", {"start": v(20.7, 51.21) * mm, "end": v(16.36, 53.03) * mm});
            skLineSegment(sketch, "E354", {"start": v(16.36, 53.03) * mm, "end": v(11.58, 54.45) * mm});
            skLineSegment(sketch, "E355", {"start": v(11.58, 54.45) * mm, "end": v(6.73, 55.4) * mm});
            skLineSegment(sketch, "E356", {"start": v(6.73, 55.4) * mm, "end": v(2.16, 55.8) * mm});
            skLineSegment(sketch, "E357", {"start": v(2.16, 55.8) * mm, "end": v(-1.76, 55.52) * mm});
            skLineSegment(sketch, "E358", {"start": v(-1.76, 55.52) * mm, "end": v(-4.67, 54.5) * mm});
            skLineSegment(sketch, "E359", {"start": v(-4.67, 54.5) * mm, "end": v(-5.7, 53.77) * mm});
            skLineSegment(sketch, "E360", {"start": v(-5.7, 53.77) * mm, "end": v(-6.8, 52.85) * mm});
            skLineSegment(sketch, "E361", {"start": v(-6.8, 52.85) * mm, "end": v(-7.93, 51.79) * mm});
            skLineSegment(sketch, "E362", {"start": v(-7.93, 51.79) * mm, "end": v(-9.02, 50.6) * mm});
            skLineSegment(sketch, "E363", {"start": v(-9.02, 50.6) * mm, "end": v(-10.03, 49.37) * mm});
            skLineSegment(sketch, "E364", {"start": v(-10.03, 49.37) * mm, "end": v(-10.92, 48.1) * mm});
            skLineSegment(sketch, "E365", {"start": v(-10.92, 48.1) * mm, "end": v(-11.63, 46.86) * mm});
            skLineSegment(sketch, "E366", {"start": v(-11.63, 46.86) * mm, "end": v(-12.12, 45.67) * mm});
            skLineSegment(sketch, "E367", {"start": v(-12.12, 45.67) * mm, "end": v(-12.24, 44.53) * mm});
            skLineSegment(sketch, "E368", {"start": v(-12.24, 44.53) * mm, "end": v(-11.96, 43.39) * mm});
            skLineSegment(sketch, "E369", {"start": v(-11.96, 43.39) * mm, "end": v(-11.34, 42.24) * mm});
            skLineSegment(sketch, "E370", {"start": v(-11.34, 42.24) * mm, "end": v(-10.47, 41.08) * mm});
            skLineSegment(sketch, "E371", {"start": v(-10.47, 41.08) * mm, "end": v(-9.42, 39.9) * mm});
            skLineSegment(sketch, "E372", {"start": v(-9.42, 39.9) * mm, "end": v(-8.28, 38.72) * mm});
            skLineSegment(sketch, "E373", {"start": v(-8.28, 38.72) * mm, "end": v(-7.13, 37.52) * mm});
            skLineSegment(sketch, "E374", {"start": v(-7.13, 37.52) * mm, "end": v(-6.04, 36.3) * mm});
            skLineSegment(sketch, "E375", {"start": v(-6.04, 36.3) * mm, "end": v(-5.61, 35.78) * mm});
            skLineSegment(sketch, "E376", {"start": v(-5.61, 35.78) * mm, "end": v(-5.18, 35.23) * mm});
            skLineSegment(sketch, "E377", {"start": v(-5.18, 35.23) * mm, "end": v(-4.74, 34.65) * mm});
            skLineSegment(sketch, "E378", {"start": v(-4.74, 34.65) * mm, "end": v(-4.3, 34.07) * mm});
            skLineSegment(sketch, "E379", {"start": v(-4.3, 34.07) * mm, "end": v(-3.84, 33.49) * mm});
            skLineSegment(sketch, "E380", {"start": v(-3.84, 33.49) * mm, "end": v(-3.4, 32.93) * mm});
            skLineSegment(sketch, "E381", {"start": v(-3.4, 32.93) * mm, "end": v(-2.95, 32.4) * mm});
            skLineSegment(sketch, "E382", {"start": v(-2.95, 32.4) * mm, "end": v(-2.5, 31.92) * mm});
            skLineSegment(sketch, "E383", {"start": v(-2.5, 31.92) * mm, "end": v(-1.78, 31.24) * mm});
            skLineSegment(sketch, "E384", {"start": v(-1.78, 31.24) * mm, "end": v(-1.12, 30.75) * mm});
            skLineSegment(sketch, "E385", {"start": v(-1.12, 30.75) * mm, "end": v(-0.46, 30.42) * mm});
            skLineSegment(sketch, "E386", {"start": v(-0.46, 30.42) * mm, "end": v(0.22, 30.22) * mm});
            skLineSegment(sketch, "E387", {"start": v(0.22, 30.22) * mm, "end": v(0.99, 30.13) * mm});
            skLineSegment(sketch, "E388", {"start": v(0.99, 30.13) * mm, "end": v(1.87, 30.13) * mm});
            skLineSegment(sketch, "E389", {"start": v(1.87, 30.13) * mm, "end": v(2.9, 30.19) * mm});
            skLineSegment(sketch, "E390", {"start": v(2.9, 30.19) * mm, "end": v(4.15, 30.28) * mm});
            skLineSegment(sketch, "E391", {"start": v(4.15, 30.28) * mm, "end": v(6.1, 30.41) * mm});
            skLineSegment(sketch, "E392", {"start": v(6.1, 30.41) * mm, "end": v(8.05, 30.54) * mm});
            skLineSegment(sketch, "E393", {"start": v(8.05, 30.54) * mm, "end": v(10.01, 30.66) * mm});
            skLineSegment(sketch, "E394", {"start": v(10.01, 30.66) * mm, "end": v(11.97, 30.8) * mm});
            skLineSegment(sketch, "E395", {"start": v(11.97, 30.8) * mm, "end": v(13.93, 30.92) * mm});
            skLineSegment(sketch, "E396", {"start": v(13.93, 30.92) * mm, "end": v(15.89, 31.07) * mm});
            skLineSegment(sketch, "E397", {"start": v(15.89, 31.07) * mm, "end": v(17.84, 31.24) * mm});
            skLineSegment(sketch, "E398", {"start": v(17.84, 31.24) * mm, "end": v(19.77, 31.43) * mm});
            skLineSegment(sketch, "E399", {"start": v(-42.94, -27.6) * mm, "end": v(-42.92, -29.86) * mm});
            skLineSegment(sketch, "E400", {"start": v(-42.92, -29.86) * mm, "end": v(-42.89, -31.62) * mm});
            skLineSegment(sketch, "E401", {"start": v(-42.89, -31.62) * mm, "end": v(-42.8, -33.01) * mm});
            skLineSegment(sketch, "E402", {"start": v(-42.8, -33.01) * mm, "end": v(-42.58, -34.16) * mm});
            skLineSegment(sketch, "E403", {"start": v(-42.58, -34.16) * mm, "end": v(-42.2, -35.2) * mm});
            skLineSegment(sketch, "E404", {"start": v(-42.2, -35.2) * mm, "end": v(-41.6, -36.23) * mm});
            skLineSegment(sketch, "E405", {"start": v(-41.6, -36.23) * mm, "end": v(-40.72, -37.38) * mm});
            skLineSegment(sketch, "E406", {"start": v(-40.72, -37.38) * mm, "end": v(-39.53, -38.78) * mm});
            skLineSegment(sketch, "E407", {"start": v(-39.53, -38.78) * mm, "end": v(-37.95, -40.4) * mm});
            skLineSegment(sketch, "E408", {"start": v(-37.95, -40.4) * mm, "end": v(-36.03, -42.12) * mm});
            skLineSegment(sketch, "E409", {"start": v(-36.03, -42.12) * mm, "end": v(-33.86, -43.86) * mm});
            skLineSegment(sketch, "E410", {"start": v(-33.86, -43.86) * mm, "end": v(-31.51, -45.56) * mm});
            skLineSegment(sketch, "E411", {"start": v(-31.51, -45.56) * mm, "end": v(-29.09, -47.16) * mm});
            skLineSegment(sketch, "E412", {"start": v(-29.09, -47.16) * mm, "end": v(-26.67, -48.6) * mm});
            skLineSegment(sketch, "E413", {"start": v(-26.67, -48.6) * mm, "end": v(-24.35, -49.83) * mm});
            skLineSegment(sketch, "E414", {"start": v(-24.35, -49.83) * mm, "end": v(-22.22, -50.78) * mm});
            skLineSegment(sketch, "E415", {"start": v(-22.22, -50.78) * mm, "end": v(-20.64, -51.3) * mm});
            skLineSegment(sketch, "E416", {"start": v(-20.64, -51.3) * mm, "end": v(-19, -51.66) * mm});
            skLineSegment(sketch, "E417", {"start": v(-19, -51.66) * mm, "end": v(-17.36, -51.84) * mm});
            skLineSegment(sketch, "E418", {"start": v(-17.36, -51.84) * mm, "end": v(-15.73, -51.83) * mm});
            skLineSegment(sketch, "E419", {"start": v(-15.73, -51.83) * mm, "end": v(-14.14, -51.63) * mm});
            skLineSegment(sketch, "E420", {"start": v(-14.14, -51.63) * mm, "end": v(-12.63, -51.23) * mm});
            skLineSegment(sketch, "E421", {"start": v(-12.63, -51.23) * mm, "end": v(-11.22, -50.62) * mm});
            skLineSegment(sketch, "E422", {"start": v(-11.22, -50.62) * mm, "end": v(-9.95, -49.8) * mm});
            skLineSegment(sketch, "E423", {"start": v(-9.95, -49.8) * mm, "end": v(-10.07, -48.57) * mm});
            skLineSegment(sketch, "E424", {"start": v(-10.07, -48.57) * mm, "end": v(-10.32, -46.96) * mm});
            skLineSegment(sketch, "E425", {"start": v(-10.32, -46.96) * mm, "end": v(-10.67, -45.12) * mm});
            skLineSegment(sketch, "E426", {"start": v(-10.67, -45.12) * mm, "end": v(-11.1, -43.19) * mm});
            skLineSegment(sketch, "E427", {"start": v(-11.1, -43.19) * mm, "end": v(-11.59, -41.33) * mm});
            skLineSegment(sketch, "E428", {"start": v(-11.59, -41.33) * mm, "end": v(-12.1, -39.7) * mm});
            skLineSegment(sketch, "E429", {"start": v(-12.1, -39.7) * mm, "end": v(-12.61, -38.44) * mm});
            skLineSegment(sketch, "E430", {"start": v(-12.61, -38.44) * mm, "end": v(-13.1, -37.71) * mm});
            skLineSegment(sketch, "E431", {"start": v(-13.1, -37.71) * mm, "end": v(-13.4, -37.5) * mm});
            skLineSegment(sketch, "E432", {"start": v(-13.4, -37.5) * mm, "end": v(-13.92, -37.19) * mm});
            skLineSegment(sketch, "E433", {"start": v(-13.92, -37.19) * mm, "end": v(-14.59, -36.8) * mm});
            skLineSegment(sketch, "E434", {"start": v(-14.59, -36.8) * mm, "end": v(-15.33, -36.39) * mm});
            skLineSegment(sketch, "E435", {"start": v(-15.33, -36.39) * mm, "end": v(-16.1, -35.96) * mm});
            skLineSegment(sketch, "E436", {"start": v(-16.1, -35.96) * mm, "end": v(-16.81, -35.55) * mm});
            skLineSegment(sketch, "E437", {"start": v(-16.81, -35.55) * mm, "end": v(-17.41, -35.2) * mm});
            skLineSegment(sketch, "E438", {"start": v(-17.41, -35.2) * mm, "end": v(-17.84, -34.92) * mm});
            skLineSegment(sketch, "E439", {"start": v(-17.84, -34.92) * mm, "end": v(-19.49, -33.75) * mm});
            skLineSegment(sketch, "E440", {"start": v(-19.49, -33.75) * mm, "end": v(-20.74, -32.83) * mm});
            skLineSegment(sketch, "E441", {"start": v(-20.74, -32.83) * mm, "end": v(-21.7, -32.08) * mm});
            skLineSegment(sketch, "E442", {"start": v(-21.7, -32.08) * mm, "end": v(-22.52, -31.42) * mm});
            skLineSegment(sketch, "E443", {"start": v(-22.52, -31.42) * mm, "end": v(-23.3, -30.78) * mm});
            skLineSegment(sketch, "E444", {"start": v(-23.3, -30.78) * mm, "end": v(-24.14, -30.07) * mm});
            skLineSegment(sketch, "E445", {"start": v(-24.14, -30.07) * mm, "end": v(-25.17, -29.21) * mm});
            skLineSegment(sketch, "E446", {"start": v(-25.17, -29.21) * mm, "end": v(-26.52, -28.14) * mm});
            skLineSegment(sketch, "E447", {"start": v(-26.52, -28.14) * mm, "end": v(-26.85, -27.86) * mm});
            skLineSegment(sketch, "E448", {"start": v(-26.85, -27.86) * mm, "end": v(-27.11, -27.6) * mm});
            skLineSegment(sketch, "E449", {"start": v(-27.11, -27.6) * mm, "end": v(-27.34, -27.37) * mm});
            skLineSegment(sketch, "E450", {"start": v(-27.34, -27.37) * mm, "end": v(-27.54, -27.15) * mm});
            skLineSegment(sketch, "E451", {"start": v(-27.54, -27.15) * mm, "end": v(-27.74, -26.93) * mm});
            skLineSegment(sketch, "E452", {"start": v(-27.74, -26.93) * mm, "end": v(-27.96, -26.7) * mm});
            skLineSegment(sketch, "E453", {"start": v(-27.96, -26.7) * mm, "end": v(-28.21, -26.46) * mm});
            skLineSegment(sketch, "E454", {"start": v(-28.21, -26.46) * mm, "end": v(-28.52, -26.2) * mm});
            skLineSegment(sketch, "E455", {"start": v(-28.52, -26.2) * mm, "end": v(-28.94, -25.9) * mm});
            skLineSegment(sketch, "E456", {"start": v(-28.94, -25.9) * mm, "end": v(-29.65, -25.4) * mm});
            skLineSegment(sketch, "E457", {"start": v(-29.65, -25.4) * mm, "end": v(-30.03, -25.15) * mm});
            skLineSegment(sketch, "E458", {"start": v(-30.03, -25.15) * mm, "end": v(-30.4, -24.92) * mm});
            skLineSegment(sketch, "E459", {"start": v(-30.4, -24.92) * mm, "end": v(-30.71, -24.74) * mm});
            skLineSegment(sketch, "E460", {"start": v(-30.71, -24.74) * mm, "end": v(-30.95, -24.63) * mm});
            skLineSegment(sketch, "E461", {"start": v(-30.95, -24.63) * mm, "end": v(-32.08, -24.47) * mm});
            skLineSegment(sketch, "E462", {"start": v(-32.08, -24.47) * mm, "end": v(-33.57, -24.6) * mm});
            skLineSegment(sketch, "E463", {"start": v(-33.57, -24.6) * mm, "end": v(-35.3, -24.94) * mm});
            skLineSegment(sketch, "E464", {"start": v(-35.3, -24.94) * mm, "end": v(-37.13, -25.44) * mm});
            skLineSegment(sketch, "E465", {"start": v(-37.13, -25.44) * mm, "end": v(-38.94, -26.03) * mm});
            skLineSegment(sketch, "E466", {"start": v(-38.94, -26.03) * mm, "end": v(-40.6, -26.63) * mm});
            skLineSegment(sketch, "E467", {"start": v(-40.6, -26.63) * mm, "end": v(-41.97, -27.18) * mm});
            skLineSegment(sketch, "E468", {"start": v(-41.97, -27.18) * mm, "end": v(-42.94, -27.6) * mm});
            skLineSegment(sketch, "E469", {"start": v(-54.3, -1.55) * mm, "end": v(-53.57, -1.82) * mm});
            skLineSegment(sketch, "E470", {"start": v(-53.57, -1.82) * mm, "end": v(-52.98, -1.88) * mm});
            skLineSegment(sketch, "E471", {"start": v(-52.98, -1.88) * mm, "end": v(-52.47, -1.76) * mm});
            skLineSegment(sketch, "E472", {"start": v(-52.47, -1.76) * mm, "end": v(-52.04, -1.49) * mm});
            skLineSegment(sketch, "E473", {"start": v(-52.04, -1.49) * mm, "end": v(-51.64, -1.1) * mm});
            skLineSegment(sketch, "E474", {"start": v(-51.64, -1.1) * mm, "end": v(-51.27, -0.62) * mm});
            skLineSegment(sketch, "E475", {"start": v(-51.27, -0.62) * mm, "end": v(-50.88, -0.1) * mm});
            skLineSegment(sketch, "E476", {"start": v(-50.88, -0.1) * mm, "end": v(-50.46, 0.44) * mm});
            skLineSegment(sketch, "E477", {"start": v(-50.46, 0.44) * mm, "end": v(-43.94, 8.18) * mm});
            skLineSegment(sketch, "E478", {"start": v(-43.94, 8.18) * mm, "end": v(-43.3, 8.98) * mm});
            skLineSegment(sketch, "E479", {"start": v(-43.3, 8.98) * mm, "end": v(-42.84, 9.53) * mm});
            skLineSegment(sketch, "E480", {"start": v(-42.84, 9.53) * mm, "end": v(-42.53, 9.94) * mm});
            skLineSegment(sketch, "E481", {"start": v(-42.53, 9.94) * mm, "end": v(-42.33, 10.3) * mm});
            skLineSegment(sketch, "E482", {"start": v(-42.33, 10.3) * mm, "end": v(-42.18, 10.72) * mm});
            skLineSegment(sketch, "E483", {"start": v(-42.18, 10.72) * mm, "end": v(-42.04, 11.3) * mm});
            skLineSegment(sketch, "E484", {"start": v(-42.04, 11.3) * mm, "end": v(-41.87, 12.14) * mm});
            skLineSegment(sketch, "E485", {"start": v(-41.87, 12.14) * mm, "end": v(-41.6, 13.35) * mm});
            skLineSegment(sketch, "E486", {"start": v(-41.6, 13.35) * mm, "end": v(-40.67, 17.18) * mm});
            skLineSegment(sketch, "E487", {"start": v(-40.67, 17.18) * mm, "end": v(-39.78, 20.22) * mm});
            skLineSegment(sketch, "E488", {"start": v(-39.78, 20.22) * mm, "end": v(-38.9, 22.7) * mm});
            skLineSegment(sketch, "E489", {"start": v(-38.9, 22.7) * mm, "end": v(-38, 24.84) * mm});
            skLineSegment(sketch, "E490", {"start": v(-38, 24.84) * mm, "end": v(-37.01, 26.84) * mm});
            skLineSegment(sketch, "E491", {"start": v(-37.01, 26.84) * mm, "end": v(-35.93, 28.93) * mm});
            skLineSegment(sketch, "E492", {"start": v(-35.93, 28.93) * mm, "end": v(-34.72, 31.3) * mm});
            skLineSegment(sketch, "E493", {"start": v(-34.72, 31.3) * mm, "end": v(-33.33, 34.2) * mm});
            skLineSegment(sketch, "E494", {"start": v(-33.33, 34.2) * mm, "end": v(-36.55, 39.45) * mm});
            skLineSegment(sketch, "E495", {"start": v(-36.55, 39.45) * mm, "end": v(-38.66, 38.7) * mm});
            skLineSegment(sketch, "E496", {"start": v(-38.66, 38.7) * mm, "end": v(-40.7, 37.18) * mm});
            skLineSegment(sketch, "E497", {"start": v(-40.7, 37.18) * mm, "end": v(-42.62, 35.1) * mm});
            skLineSegment(sketch, "E498", {"start": v(-42.62, 35.1) * mm, "end": v(-44.43, 32.63) * mm});
            skLineSegment(sketch, "E499", {"start": v(-44.43, 32.63) * mm, "end": v(-46.09, 29.97) * mm});
            skLineSegment(sketch, "E500", {"start": v(-46.09, 29.97) * mm, "end": v(-47.56, 27.33) * mm});
            skLineSegment(sketch, "E501", {"start": v(-47.56, 27.33) * mm, "end": v(-48.83, 24.88) * mm});
            skLineSegment(sketch, "E502", {"start": v(-48.83, 24.88) * mm, "end": v(-49.86, 22.81) * mm});
            skLineSegment(sketch, "E503", {"start": v(-49.86, 22.81) * mm, "end": v(-51.07, 20.23) * mm});
            skLineSegment(sketch, "E504", {"start": v(-51.07, 20.23) * mm, "end": v(-52.19, 17.41) * mm});
            skLineSegment(sketch, "E505", {"start": v(-52.19, 17.41) * mm, "end": v(-53.17, 14.42) * mm});
            skLineSegment(sketch, "E506", {"start": v(-53.17, 14.42) * mm, "end": v(-53.97, 11.29) * mm});
            skLineSegment(sketch, "E507", {"start": v(-53.97, 11.29) * mm, "end": v(-54.53, 8.07) * mm});
            skLineSegment(sketch, "E508", {"start": v(-54.53, 8.07) * mm, "end": v(-54.8, 4.83) * mm});
            skLineSegment(sketch, "E509", {"start": v(-54.8, 4.83) * mm, "end": v(-54.74, 1.6) * mm});
            skLineSegment(sketch, "E510", {"start": v(-54.74, 1.6) * mm, "end": v(-54.3, -1.55) * mm});
            skLineSegment(sketch, "E511", {"start": v(15.14, -49.8) * mm, "end": v(17.04, -51.22) * mm});
            skLineSegment(sketch, "E512", {"start": v(17.04, -51.22) * mm, "end": v(19.65, -51.36) * mm});
            skLineSegment(sketch, "E513", {"start": v(19.65, -51.36) * mm, "end": v(22.7, -50.53) * mm});
            skLineSegment(sketch, "E514", {"start": v(22.7, -50.53) * mm, "end": v(25.94, -49.03) * mm});
            skLineSegment(sketch, "E515", {"start": v(25.94, -49.03) * mm, "end": v(29.12, -47.18) * mm});
            skLineSegment(sketch, "E516", {"start": v(29.12, -47.18) * mm, "end": v(31.96, -45.26) * mm});
            skLineSegment(sketch, "E517", {"start": v(31.96, -45.26) * mm, "end": v(34.23, -43.6) * mm});
            skLineSegment(sketch, "E518", {"start": v(34.23, -43.6) * mm, "end": v(35.66, -42.5) * mm});
            skLineSegment(sketch, "E519", {"start": v(35.66, -42.5) * mm, "end": v(37.63, -40.9) * mm});
            skLineSegment(sketch, "E520", {"start": v(37.63, -40.9) * mm, "end": v(39.6, -39.15) * mm});
            skLineSegment(sketch, "E521", {"start": v(39.6, -39.15) * mm, "end": v(41.54, -37.24) * mm});
            skLineSegment(sketch, "E522", {"start": v(41.54, -37.24) * mm, "end": v(43.4, -35.15) * mm});
            skLineSegment(sketch, "E523", {"start": v(43.4, -35.15) * mm, "end": v(45.11, -32.83) * mm});
            skLineSegment(sketch, "E524", {"start": v(45.11, -32.83) * mm, "end": v(46.66, -30.29) * mm});
            skLineSegment(sketch, "E525", {"start": v(46.66, -30.29) * mm, "end": v(47.98, -27.49) * mm});
            skLineSegment(sketch, "E526", {"start": v(47.98, -27.49) * mm, "end": v(49.04, -24.4) * mm});
            skLineSegment(sketch, "E527", {"start": v(49.04, -24.4) * mm, "end": v(47.16, -24.2) * mm});
            skLineSegment(sketch, "E528", {"start": v(47.16, -24.2) * mm, "end": v(45.83, -24.13) * mm});
            skLineSegment(sketch, "E529", {"start": v(45.83, -24.13) * mm, "end": v(44.85, -24.23) * mm});
            skLineSegment(sketch, "E530", {"start": v(44.85, -24.23) * mm, "end": v(44.04, -24.53) * mm});
            skLineSegment(sketch, "E531", {"start": v(44.04, -24.53) * mm, "end": v(43.22, -25.06) * mm});
            skLineSegment(sketch, "E532", {"start": v(43.22, -25.06) * mm, "end": v(42.2, -25.83) * mm});
            skLineSegment(sketch, "E533", {"start": v(42.2, -25.83) * mm, "end": v(40.81, -26.88) * mm});
            skLineSegment(sketch, "E534", {"start": v(40.81, -26.88) * mm, "end": v(38.85, -28.24) * mm});
            skLineSegment(sketch, "E535", {"start": v(38.85, -28.24) * mm, "end": v(37.8, -28.97) * mm});
            skLineSegment(sketch, "E536", {"start": v(37.8, -28.97) * mm, "end": v(36.74, -29.75) * mm});
            skLineSegment(sketch, "E537", {"start": v(36.74, -29.75) * mm, "end": v(35.69, -30.55) * mm});
            skLineSegment(sketch, "E538", {"start": v(35.69, -30.55) * mm, "end": v(34.63, -31.38) * mm});
            skLineSegment(sketch, "E539", {"start": v(34.63, -31.38) * mm, "end": v(33.56, -32.21) * mm});
            skLineSegment(sketch, "E540", {"start": v(33.56, -32.21) * mm, "end": v(32.46, -33.04) * mm});
            skLineSegment(sketch, "E541", {"start": v(32.46, -33.04) * mm, "end": v(31.34, -33.85) * mm});
            skLineSegment(sketch, "E542", {"start": v(31.34, -33.85) * mm, "end": v(30.17, -34.63) * mm});
            skLineSegment(sketch, "E543", {"start": v(30.17, -34.63) * mm, "end": v(28.83, -35.44) * mm});
            skLineSegment(sketch, "E544", {"start": v(28.83, -35.44) * mm, "end": v(27.66, -36.1) * mm});
            skLineSegment(sketch, "E545", {"start": v(27.66, -36.1) * mm, "end": v(26.62, -36.68) * mm});
            skLineSegment(sketch, "E546", {"start": v(26.62, -36.68) * mm, "end": v(25.66, -37.25) * mm});
            skLineSegment(sketch, "E547", {"start": v(25.66, -37.25) * mm, "end": v(24.72, -37.9) * mm});
            skLineSegment(sketch, "E548", {"start": v(24.72, -37.9) * mm, "end": v(23.76, -38.7) * mm});
            skLineSegment(sketch, "E549", {"start": v(23.76, -38.7) * mm, "end": v(22.72, -39.73) * mm});
            skLineSegment(sketch, "E550", {"start": v(22.72, -39.73) * mm, "end": v(21.56, -41.06) * mm});
            skLineSegment(sketch, "E551", {"start": v(21.56, -41.06) * mm, "end": v(20.9, -41.87) * mm});
            skLineSegment(sketch, "E552", {"start": v(20.9, -41.87) * mm, "end": v(20.08, -42.9) * mm});
            skLineSegment(sketch, "E553", {"start": v(20.08, -42.9) * mm, "end": v(19.16, -44.05) * mm});
            skLineSegment(sketch, "E554", {"start": v(19.16, -44.05) * mm, "end": v(18.2, -45.3) * mm});
            skLineSegment(sketch, "E555", {"start": v(18.2, -45.3) * mm, "end": v(17.27, -46.55) * mm});
            skLineSegment(sketch, "E556", {"start": v(17.27, -46.55) * mm, "end": v(16.4, -47.76) * mm});
            skLineSegment(sketch, "E557", {"start": v(16.4, -47.76) * mm, "end": v(15.68, -48.87) * mm});
            skLineSegment(sketch, "E558", {"start": v(15.68, -48.87) * mm, "end": v(15.14, -49.8) * mm});
            skLineSegment(sketch, "E559", {"start": v(-12.45, -53.72) * mm, "end": v(-9.44, -54.66) * mm});
            skLineSegment(sketch, "E560", {"start": v(-9.44, -54.66) * mm, "end": v(-6.21, -55.25) * mm});
            skLineSegment(sketch, "E561", {"start": v(-6.21, -55.25) * mm, "end": v(-2.85, -55.54) * mm});
            skLineSegment(sketch, "E562", {"start": v(-2.85, -55.54) * mm, "end": v(0.6, -55.56) * mm});
            skLineSegment(sketch, "E563", {"start": v(0.6, -55.56) * mm, "end": v(4.04, -55.35) * mm});
            skLineSegment(sketch, "E564", {"start": v(4.04, -55.35) * mm, "end": v(7.42, -54.94) * mm});
            skLineSegment(sketch, "E565", {"start": v(7.42, -54.94) * mm, "end": v(10.67, -54.38) * mm});
            skLineSegment(sketch, "E566", {"start": v(10.67, -54.38) * mm, "end": v(13.71, -53.7) * mm});
            skLineSegment(sketch, "E567", {"start": v(13.71, -53.7) * mm, "end": v(11.48, -52.83) * mm});
            skLineSegment(sketch, "E568", {"start": v(11.48, -52.83) * mm, "end": v(8.32, -52.18) * mm});
            skLineSegment(sketch, "E569", {"start": v(8.32, -52.18) * mm, "end": v(4.55, -51.76) * mm});
            skLineSegment(sketch, "E570", {"start": v(4.55, -51.76) * mm, "end": v(0.5, -51.6) * mm});
            skLineSegment(sketch, "E571", {"start": v(0.5, -51.6) * mm, "end": v(-3.55, -51.69) * mm});
            skLineSegment(sketch, "E572", {"start": v(-3.55, -51.69) * mm, "end": v(-7.26, -52.06) * mm});
            skLineSegment(sketch, "E573", {"start": v(-7.26, -52.06) * mm, "end": v(-10.34, -52.74) * mm});
            skLineSegment(sketch, "E574", {"start": v(-10.34, -52.74) * mm, "end": v(-12.45, -53.72) * mm});
            skLineSegment(sketch, "E575", {"start": v(-44.96, -31.52) * mm, "end": v(-44.9, -29.84) * mm});
            skLineSegment(sketch, "E576", {"start": v(-44.9, -29.84) * mm, "end": v(-45.1, -28.3) * mm});
            skLineSegment(sketch, "E577", {"start": v(-45.1, -28.3) * mm, "end": v(-45.52, -26.84) * mm});
            skLineSegment(sketch, "E578", {"start": v(-45.52, -26.84) * mm, "end": v(-46.14, -25.36) * mm});
            skLineSegment(sketch, "E579", {"start": v(-46.14, -25.36) * mm, "end": v(-46.9, -23.81) * mm});
            skLineSegment(sketch, "E580", {"start": v(-46.9, -23.81) * mm, "end": v(-47.75, -22.1) * mm});
            skLineSegment(sketch, "E581", {"start": v(-47.75, -22.1) * mm, "end": v(-48.65, -20.16) * mm});
            skLineSegment(sketch, "E582", {"start": v(-48.65, -20.16) * mm, "end": v(-49.58, -17.91) * mm});
            skLineSegment(sketch, "E583", {"start": v(-49.58, -17.91) * mm, "end": v(-50.06, -16.6) * mm});
            skLineSegment(sketch, "E584", {"start": v(-50.06, -16.6) * mm, "end": v(-50.54, -15.28) * mm});
            skLineSegment(sketch, "E585", {"start": v(-50.54, -15.28) * mm, "end": v(-51, -13.93) * mm});
            skLineSegment(sketch, "E586", {"start": v(-51, -13.93) * mm, "end": v(-51.41, -12.57) * mm});
            skLineSegment(sketch, "E587", {"start": v(-51.41, -12.57) * mm, "end": v(-51.78, -11.2) * mm});
            skLineSegment(sketch, "E588", {"start": v(-51.78, -11.2) * mm, "end": v(-52.1, -9.81) * mm});
            skLineSegment(sketch, "E589", {"start": v(-52.1, -9.81) * mm, "end": v(-52.35, -8.42) * mm});
            skLineSegment(sketch, "E590", {"start": v(-52.35, -8.42) * mm, "end": v(-52.52, -7.01) * mm});
            skLineSegment(sketch, "E591", {"start": v(-52.52, -7.01) * mm, "end": v(-52.57, -6.29) * mm});
            skLineSegment(sketch, "E592", {"start": v(-52.57, -6.29) * mm, "end": v(-52.58, -5.68) * mm});
            skLineSegment(sketch, "E593", {"start": v(-52.58, -5.68) * mm, "end": v(-52.6, -5.18) * mm});
            skLineSegment(sketch, "E594", {"start": v(-52.6, -5.18) * mm, "end": v(-52.67, -4.77) * mm});
            skLineSegment(sketch, "E595", {"start": v(-52.67, -4.77) * mm, "end": v(-52.82, -4.44) * mm});
            skLineSegment(sketch, "E596", {"start": v(-52.82, -4.44) * mm, "end": v(-53.09, -4.19) * mm});
            skLineSegment(sketch, "E597", {"start": v(-53.09, -4.19) * mm, "end": v(-53.5, -3.98) * mm});
            skLineSegment(sketch, "E598", {"start": v(-53.5, -3.98) * mm, "end": v(-54.1, -3.82) * mm});
            skLineSegment(sketch, "E599", {"start": v(-54.1, -3.82) * mm, "end": v(-54.15, -3.88) * mm});
            skLineSegment(sketch, "E600", {"start": v(-54.15, -3.88) * mm, "end": v(-54.18, -3.94) * mm});
            skLineSegment(sketch, "E601", {"start": v(-54.18, -3.94) * mm, "end": v(-54.21, -4) * mm});
            skLineSegment(sketch, "E602", {"start": v(-54.21, -4) * mm, "end": v(-54.23, -4.1) * mm});
            skLineSegment(sketch, "E603", {"start": v(-54.23, -4.1) * mm, "end": v(-54.4, -6.32) * mm});
            skLineSegment(sketch, "E604", {"start": v(-54.4, -6.32) * mm, "end": v(-54.44, -8.22) * mm});
            skLineSegment(sketch, "E605", {"start": v(-54.44, -8.22) * mm, "end": v(-54.37, -9.91) * mm});
            skLineSegment(sketch, "E606", {"start": v(-54.37, -9.91) * mm, "end": v(-54.17, -11.51) * mm});
            skLineSegment(sketch, "E607", {"start": v(-54.17, -11.51) * mm, "end": v(-53.8, -13.13) * mm});
            skLineSegment(sketch, "E608", {"start": v(-53.8, -13.13) * mm, "end": v(-53.28, -14.88) * mm});
            skLineSegment(sketch, "E609", {"start": v(-53.28, -14.88) * mm, "end": v(-52.58, -16.88) * mm});
            skLineSegment(sketch, "E610", {"start": v(-52.58, -16.88) * mm, "end": v(-51.68, -19.24) * mm});
            skLineSegment(sketch, "E611", {"start": v(-51.68, -19.24) * mm, "end": v(-51.13, -20.6) * mm});
            skLineSegment(sketch, "E612", {"start": v(-51.13, -20.6) * mm, "end": v(-50.4, -22.24) * mm});
            skLineSegment(sketch, "E613", {"start": v(-50.4, -22.24) * mm, "end": v(-49.55, -24.06) * mm});
            skLineSegment(sketch, "E614", {"start": v(-49.55, -24.06) * mm, "end": v(-48.62, -25.94) * mm});
            skLineSegment(sketch, "E615", {"start": v(-48.62, -25.94) * mm, "end": v(-47.64, -27.74) * mm});
            skLineSegment(sketch, "E616", {"start": v(-47.64, -27.74) * mm, "end": v(-46.68, -29.35) * mm});
            skLineSegment(sketch, "E617", {"start": v(-46.68, -29.35) * mm, "end": v(-45.77, -30.65) * mm});
            skLineSegment(sketch, "E618", {"start": v(-45.77, -30.65) * mm, "end": v(-44.96, -31.52) * mm});
            skSolve(sketch);
        }
        {
            var Q0;
            Q0=makeQuery(id+"F0.imprint","IMPRINT",FACE,{"disambiguationData":[TD([[makeQuery(id+"F0.imprint","IMPRINT",EDGE,{"derivedFrom":sQuery(id+"F0.wireOp",EDGE,"E0")}),1.0]])]});
            extrude(context, id + "F1", {"entities" : qUnion([Q0]), "depth" : 19.05 * mm, "offsetDistance" : 25.4 * mm});
        }
    });
